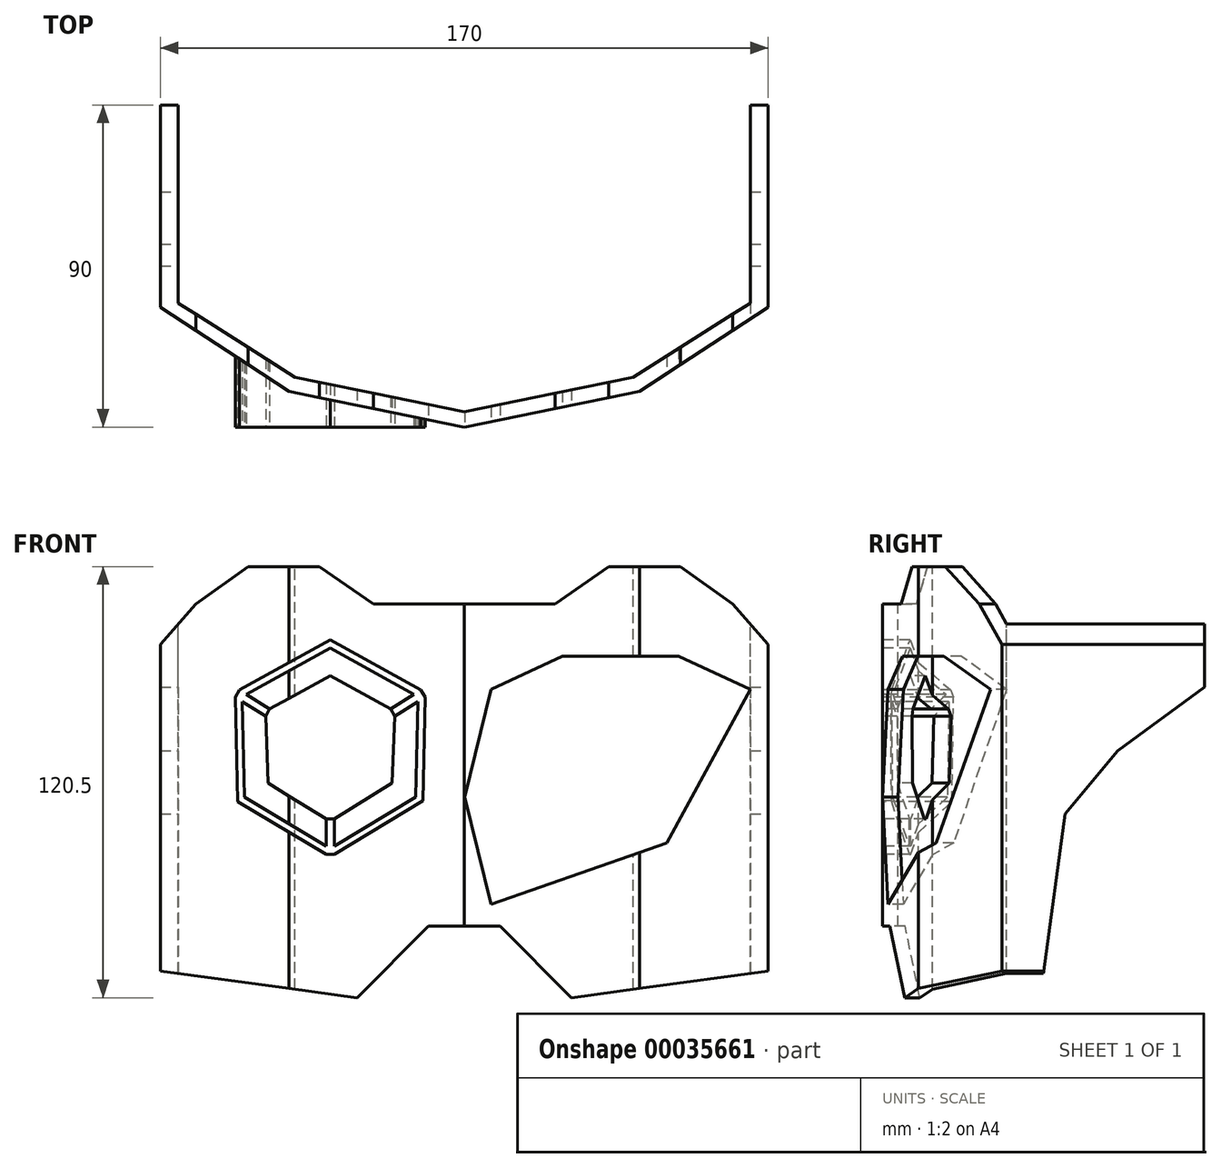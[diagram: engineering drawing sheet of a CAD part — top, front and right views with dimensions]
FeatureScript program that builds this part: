
annotation { "Feature Type Name" : "Feature", "Feature Type Description" : "" }
export const myFeature = defineFeature(function(context is Context, id is Id, definition is map)
    precondition{}
    {
        {
            var Q0;
            Q0=qCreatedBy(makeId("Front.planeOp"),FACE);
            var sketch = newSketch(context, id + "F0", { "sketchPlane" : qUnion([Q0])});
            skLineSegment(sketch, "E0.bottom", {"start": v(-25.45, 110) * mm, "end": v(25.45, 110) * mm});
            skLineSegment(sketch, "E0.top", {"start": v(-85, 0) * mm, "end": v(85, 0) * mm});
            skLineSegment(sketch, "E0.left", {"start": v(-85, 98.76) * mm, "end": v(-85, 0) * mm});
            skLineSegment(sketch, "E0.right", {"start": v(85, 98.76) * mm, "end": v(85, 0) * mm});
            skLineSegment(sketch, "E1", {"start": v(-85, 98.76) * mm, "end": v(-75.07, 110) * mm});
            skLineSegment(sketch, "E2", {"start": v(75.07, 110) * mm, "end": v(85, 98.76) * mm});
            skLineSegment(sketch, "E3", {"start": v(-85, 7.5) * mm, "end": v(-30, 0) * mm});
            skLineSegment(sketch, "E4", {"start": v(-30, 0) * mm, "end": v(-10, 20) * mm});
            skLineSegment(sketch, "E5", {"start": v(-10, 20) * mm, "end": v(10, 20) * mm});
            skLineSegment(sketch, "E6", {"start": v(10, 20) * mm, "end": v(30, 0) * mm});
            skLineSegment(sketch, "E7", {"start": v(30, 0) * mm, "end": v(85, 7.5) * mm});
            skLineSegment(sketch, "E8", {"start": v(-75.07, 110) * mm, "end": v(-60.45, 120.5) * mm});
            skLineSegment(sketch, "E9", {"start": v(-60.45, 120.5) * mm, "end": v(-40.45, 120.5) * mm});
            skLineSegment(sketch, "E10", {"start": v(-40.45, 120.5) * mm, "end": v(-25.45, 110) * mm});
            skLineSegment(sketch, "E11", {"start": v(25.45, 110) * mm, "end": v(40.45, 120.5) * mm});
            skLineSegment(sketch, "E12", {"start": v(40.45, 120.5) * mm, "end": v(60.45, 120.5) * mm});
            skLineSegment(sketch, "E13", {"start": v(60.45, 120.5) * mm, "end": v(75.07, 110) * mm});
            skSolve(sketch);
        }
        {
            var Q0;
            Q0=makeQuery(id+"F0.imprint","IMPRINT",FACE,{"disambiguationData":[TD([[makeQuery(id+"F0.imprint","IMPRINT",EDGE,{"derivedFrom":sQuery(id+"F0.wireOp",EDGE,"E0.bottom")}),-1.0]])]});
            extrude(context, id + "F1", {"entities" : qUnion([Q0]), "oppositeDirection" : true, "depth" : 90 * mm});
        }
        {
            var Q0;
            Q0=makeQuery(id+"F1.opExtrude","CAP_FACE",FACE,{"disambiguationData":[OSD([sQuery(id+"F0.wireOp",EDGE,"E0.bottom"),sQuery(id+"F0.wireOp",EDGE,"E0.left"),sQuery(id+"F0.wireOp",EDGE,"E0.right"),sQuery(id+"F0.wireOp",EDGE,"E1"),sQuery(id+"F0.wireOp",EDGE,"E2"),sQuery(id+"F0.wireOp",EDGE,"E3"),sQuery(id+"F0.wireOp",EDGE,"E4"),sQuery(id+"F0.wireOp",EDGE,"E5"),sQuery(id+"F0.wireOp",EDGE,"E6"),sQuery(id+"F0.wireOp",EDGE,"E7"),sQuery(id+"F0.wireOp",EDGE,"E8"),sQuery(id+"F0.wireOp",EDGE,"E9"),sQuery(id+"F0.wireOp",EDGE,"E10"),sQuery(id+"F0.wireOp",EDGE,"E11"),sQuery(id+"F0.wireOp",EDGE,"E12"),sQuery(id+"F0.wireOp",EDGE,"E13")])],"isStart":true});
            var sketch = newSketch(context, id + "F2", { "sketchPlane" : qUnion([Q0])});
            skCircle(sketch, "E14", {"center": v(-37.5, 70) * mm, "radius": 30 * mm, "construction": true});
            skCircle(sketch, "E15", {"center": v(-37.5, 70) * mm, "radius": 20 * mm, "construction": true});
            skLineSegment(sketch, "E16", {"start": v(-20.58, 80.67) * mm, "end": v(-14.08, 84.77) * mm});
            skPoint(sketch, "E17", {"position": v(-7.5, 70) * mm});
            skPoint(sketch, "E18", {"position": v(-67.5, 70) * mm});
            skLineSegment(sketch, "E19", {"start": v(7.5, 86.14) * mm, "end": v(27.5, 95.5) * mm});
            skLineSegment(sketch, "E20", {"start": v(27.5, 95.5) * mm, "end": v(60, 95.5) * mm});
            skLineSegment(sketch, "E21", {"start": v(60, 95.5) * mm, "end": v(80, 86.14) * mm});
            skLineSegment(sketch, "E22", {"start": v(-19.46, 78.64) * mm, "end": v(-12.93, 82.76) * mm});
            skLineSegment(sketch, "E23", {"start": v(-54.42, 80.67) * mm, "end": v(-60.92, 84.77) * mm});
            skLineSegment(sketch, "E24", {"start": v(-55.53, 78.65) * mm, "end": v(-62.07, 82.77) * mm});
            skLineSegment(sketch, "E25", {"start": v(-36.34, 50.03) * mm, "end": v(-36.34, 42.33) * mm});
            skLineSegment(sketch, "E26", {"start": v(-38.65, 50.03) * mm, "end": v(-38.65, 42.33) * mm});
            skArc(sketch, "E27.0", {"start": v(-62.07, 82.77) * mm, "mid": v(-61.46, 56.12) * mm, "end": v(-38.66, 42.33) * mm, "construction": true});
            skPoint(sketch, "E28.orphan", {"position": v(-64.03, 84) * mm});
            skPoint(sketch, "E29.orphan", {"position": v(-62.87, 86) * mm});
            skArc(sketch, "E30.trimOffspring", {"start": v(-14.08, 84.77) * mm, "mid": v(-37.5, 97.69) * mm, "end": v(-60.92, 84.77) * mm, "construction": true});
            skPoint(sketch, "E31.orphan", {"position": v(-12.12, 86) * mm});
            skPoint(sketch, "E32.orphan", {"position": v(-10.97, 84) * mm});
            skPoint(sketch, "E33.orphan", {"position": v(-36.35, 40.02) * mm});
            skPoint(sketch, "E34.orphan", {"position": v(-38.66, 40.02) * mm});
            skArc(sketch, "E35.trimOffspring", {"start": v(-36.35, 42.33) * mm, "mid": v(-13.54, 56.12) * mm, "end": v(-12.93, 82.76) * mm, "construction": true});
            skLineSegment(sketch, "E36", {"start": v(-37.5, 70) * mm, "end": v(-37.5, 97.7) * mm, "construction": true});
            skLineSegment(sketch, "E37", {"start": v(-37.5, 70) * mm, "end": v(-13.54, 56.12) * mm, "construction": true});
            skLineSegment(sketch, "E38", {"start": v(-37.5, 70) * mm, "end": v(-61.46, 56.12) * mm, "construction": true});
            skLineSegment(sketch, "E39", {"start": v(7.5, 26.14) * mm, "end": v(56.63, 43.24) * mm});
            skLineSegment(sketch, "E40", {"start": v(56.63, 43.24) * mm, "end": v(80, 86.14) * mm});
            skLineSegment(sketch, "E41", {"start": v(7.5, 26.14) * mm, "end": v(0.16, 56.14) * mm});
            skLineSegment(sketch, "E42", {"start": v(0.16, 56.14) * mm, "end": v(7.5, 86.14) * mm});
            skLineSegment(sketch, "E43", {"start": v(-36.35, 42.33) * mm, "end": v(-13.54, 56.12) * mm});
            skLineSegment(sketch, "E44", {"start": v(-12.93, 82.76) * mm, "end": v(-13.54, 56.12) * mm});
            skLineSegment(sketch, "E45", {"start": v(-14.08, 84.77) * mm, "end": v(-37.5, 97.7) * mm});
            skLineSegment(sketch, "E46", {"start": v(-60.92, 84.77) * mm, "end": v(-37.5, 97.7) * mm});
            skLineSegment(sketch, "E47", {"start": v(-38.66, 42.33) * mm, "end": v(-61.46, 56.12) * mm});
            skLineSegment(sketch, "E48", {"start": v(-61.46, 56.12) * mm, "end": v(-62.07, 82.77) * mm});
            skLineSegment(sketch, "E49", {"start": v(-64.03, 84) * mm, "end": v(-63.36, 54.8) * mm});
            skLineSegment(sketch, "E50", {"start": v(-63.36, 54.8) * mm, "end": v(-38.66, 40.02) * mm});
            skLineSegment(sketch, "E51", {"start": v(-36.35, 40.02) * mm, "end": v(-11.5, 55.05) * mm});
            skLineSegment(sketch, "E52", {"start": v(-11.5, 55.05) * mm, "end": v(-10.97, 84) * mm});
            skLineSegment(sketch, "E53", {"start": v(-62.87, 86) * mm, "end": v(-37.5, 100) * mm});
            skLineSegment(sketch, "E54", {"start": v(-37.5, 100) * mm, "end": v(-12.12, 86) * mm});
            skLineSegment(sketch, "E55", {"start": v(-36.35, 50.03) * mm, "end": v(-20.2, 59.98) * mm});
            skLineSegment(sketch, "E56", {"start": v(-20.2, 59.98) * mm, "end": v(-19.46, 78.64) * mm});
            skLineSegment(sketch, "E57", {"start": v(-38.66, 50.03) * mm, "end": v(-54.8, 59.98) * mm});
            skLineSegment(sketch, "E58", {"start": v(-54.8, 59.98) * mm, "end": v(-55.53, 78.65) * mm});
            skLineSegment(sketch, "E59", {"start": v(-54.42, 80.67) * mm, "end": v(-37.5, 90) * mm});
            skLineSegment(sketch, "E60", {"start": v(-37.5, 90) * mm, "end": v(-20.58, 80.67) * mm});
            skLineSegment(sketch, "E61", {"start": v(-55.53, 78.65) * mm, "end": v(-54.42, 80.67) * mm, "construction": true});
            skLineSegment(sketch, "E62", {"start": v(-20.58, 80.67) * mm, "end": v(-19.46, 78.64) * mm, "construction": true});
            skLineSegment(sketch, "E63", {"start": v(-38.66, 50.03) * mm, "end": v(-36.35, 50.03) * mm});
            skLineSegment(sketch, "E64", {"start": v(-55.53, 78.65) * mm, "end": v(-54.42, 80.67) * mm});
            skLineSegment(sketch, "E65", {"start": v(-20.58, 80.67) * mm, "end": v(-19.46, 78.64) * mm});
            skLineSegment(sketch, "E66", {"start": v(-38.66, 40.02) * mm, "end": v(-36.35, 40.02) * mm});
            skLineSegment(sketch, "E67", {"start": v(-10.97, 84) * mm, "end": v(-12.12, 86) * mm});
            skLineSegment(sketch, "E68", {"start": v(-64.03, 84) * mm, "end": v(-62.87, 86) * mm});
            skSolve(sketch);
        }
        {
            var Q0;
            Q0=makeQuery(id+"F2.imprint","IMPRINT",FACE,{"disambiguationData":[TD([[makeQuery(id+"F2.imprint","IMPRINT",EDGE,{"derivedFrom":sQuery(id+"F2.wireOp",EDGE,"E19")}),-1.0]])]});
            var Q1;
            Q1=makeQuery(id+"F1.opExtrude","CAP_FACE",FACE,{"disambiguationData":[OSD([sQuery(id+"F0.wireOp",EDGE,"E0.bottom"),sQuery(id+"F0.wireOp",EDGE,"E0.left"),sQuery(id+"F0.wireOp",EDGE,"E0.right"),sQuery(id+"F0.wireOp",EDGE,"E1"),sQuery(id+"F0.wireOp",EDGE,"E2"),sQuery(id+"F0.wireOp",EDGE,"E3"),sQuery(id+"F0.wireOp",EDGE,"E4"),sQuery(id+"F0.wireOp",EDGE,"E5"),sQuery(id+"F0.wireOp",EDGE,"E6"),sQuery(id+"F0.wireOp",EDGE,"E7"),sQuery(id+"F0.wireOp",EDGE,"E8"),sQuery(id+"F0.wireOp",EDGE,"E9"),sQuery(id+"F0.wireOp",EDGE,"E10"),sQuery(id+"F0.wireOp",EDGE,"E11"),sQuery(id+"F0.wireOp",EDGE,"E12"),sQuery(id+"F0.wireOp",EDGE,"E13")])],"isStart":false});
            extrude(context, id + "F3", {"entities" : qUnion([Q0]), "operationType" : NewBodyOperationType.REMOVE, "endBound" : BoundingType.UP_TO_SURFACE, "oppositeDirection" : true, "endBoundEntityFace" : qUnion([Q1]), "depth" : 25 * mm});
        }
        {
            var Q0;
            Q0=makeQuery(id+"F2.imprint","IMPRINT",FACE,{"disambiguationData":[TD([[makeQuery(id+"F2.imprint","IMPRINT",EDGE,{"derivedFrom":sQuery(id+"F2.wireOp",EDGE,"E55")}),1.0]])]});
            var Q1;
            Q1=makeQuery(id+"F1.opExtrude","CAP_FACE",FACE,{"disambiguationData":[OSD([sQuery(id+"F0.wireOp",EDGE,"E0.bottom"),sQuery(id+"F0.wireOp",EDGE,"E0.left"),sQuery(id+"F0.wireOp",EDGE,"E0.right"),sQuery(id+"F0.wireOp",EDGE,"E1"),sQuery(id+"F0.wireOp",EDGE,"E2"),sQuery(id+"F0.wireOp",EDGE,"E3"),sQuery(id+"F0.wireOp",EDGE,"E4"),sQuery(id+"F0.wireOp",EDGE,"E5"),sQuery(id+"F0.wireOp",EDGE,"E6"),sQuery(id+"F0.wireOp",EDGE,"E7"),sQuery(id+"F0.wireOp",EDGE,"E8"),sQuery(id+"F0.wireOp",EDGE,"E9"),sQuery(id+"F0.wireOp",EDGE,"E10"),sQuery(id+"F0.wireOp",EDGE,"E11"),sQuery(id+"F0.wireOp",EDGE,"E12"),sQuery(id+"F0.wireOp",EDGE,"E13")])],"isStart":false});
            extrude(context, id + "F4", {"entities" : qUnion([Q0]), "operationType" : NewBodyOperationType.REMOVE, "endBound" : BoundingType.UP_TO_SURFACE, "oppositeDirection" : true, "endBoundEntityFace" : qUnion([Q1]), "depth" : 25 * mm});
        }
        {
            var Q0;
            Q0=makeQuery(id+"F1.opExtrude","SWEPT_FACE",FACE,{"disambiguationData":[OSD([sQuery(id+"F0.wireOp",EDGE,"E9")])]});
            var sketch = newSketch(context, id + "F5", { "sketchPlane" : qUnion([Q0])});
            skLineSegment(sketch, "E69", {"start": v(85, 33.43) * mm, "end": v(85, 90) * mm});
            skLineSegment(sketch, "E70", {"start": v(85, 90) * mm, "end": v(80, 90) * mm});
            skLineSegment(sketch, "E71", {"start": v(80, 90) * mm, "end": v(80, 34.67) * mm});
            skLineSegment(sketch, "E72", {"start": v(-85, 90) * mm, "end": v(-80, 90) * mm});
            skLineSegment(sketch, "E73", {"start": v(-80, 90) * mm, "end": v(-80, 34.67) * mm});
            skLineSegment(sketch, "E74", {"start": v(-85, 90) * mm, "end": v(-85, 33.43) * mm});
            skLineSegment(sketch, "E75", {"start": v(-85, 33.43) * mm, "end": v(-48.99, 10.02) * mm});
            skLineSegment(sketch, "E76", {"start": v(-48.99, 10.02) * mm, "end": v(0, 0) * mm});
            skLineSegment(sketch, "E77", {"start": v(0, 0) * mm, "end": v(48.99, 10.02) * mm});
            skLineSegment(sketch, "E78", {"start": v(48.99, 10.02) * mm, "end": v(85, 33.43) * mm});
            skLineSegment(sketch, "E79", {"start": v(-80, 34.67) * mm, "end": v(-47.3, 13.95) * mm});
            skLineSegment(sketch, "E80", {"start": v(-47.3, 13.95) * mm, "end": v(0, 4.28) * mm});
            skLineSegment(sketch, "E81", {"start": v(0, 4.28) * mm, "end": v(47.3, 13.95) * mm});
            skLineSegment(sketch, "E82", {"start": v(47.3, 13.95) * mm, "end": v(80, 34.67) * mm});
            skSolve(sketch);
        }
        {
            var Q0;
            Q0=qSketchRegion(id+"F5",true);
            var Q1;
            Q1=qCreatedBy(makeId("Top.planeOp"),FACE);
            extrude(context, id + "F6", {"entities" : qUnion([Q0]), "operationType" : NewBodyOperationType.INTERSECT, "endBound" : BoundingType.UP_TO_SURFACE, "oppositeDirection" : true, "endBoundEntityFace" : qUnion([Q1]), "depth" : 25 * mm});
        }
        {
            var Q0;
            Q0=makeQuery(id+"F2.imprint","IMPRINT",FACE,{"disambiguationData":[TD([[makeQuery(id+"F2.imprint","IMPRINT",EDGE,{"derivedFrom":sQuery(id+"F2.wireOp",EDGE,"E16")}),-1.0]])]});
            var Q1;
            Q1=makeQuery(id+"F1.opExtrude","SWEPT_BODY",BODY,{"disambiguationData":[OSD([sQuery(id+"F0.wireOp",EDGE,"E0.bottom"),sQuery(id+"F0.wireOp",EDGE,"E0.left"),sQuery(id+"F0.wireOp",EDGE,"E0.right"),sQuery(id+"F0.wireOp",EDGE,"E1"),sQuery(id+"F0.wireOp",EDGE,"E2"),sQuery(id+"F0.wireOp",EDGE,"E3"),sQuery(id+"F0.wireOp",EDGE,"E4"),sQuery(id+"F0.wireOp",EDGE,"E5"),sQuery(id+"F0.wireOp",EDGE,"E6"),sQuery(id+"F0.wireOp",EDGE,"E7"),sQuery(id+"F0.wireOp",EDGE,"E8"),sQuery(id+"F0.wireOp",EDGE,"E9"),sQuery(id+"F0.wireOp",EDGE,"E10"),sQuery(id+"F0.wireOp",EDGE,"E11"),sQuery(id+"F0.wireOp",EDGE,"E12"),sQuery(id+"F0.wireOp",EDGE,"E13")])]});
            extrude(context, id + "F7", {"entities" : qUnion([Q0]), "operationType" : NewBodyOperationType.ADD, "endBound" : BoundingType.UP_TO_NEXT, "oppositeDirection" : true, "endBoundEntityBody" : qUnion([Q1]), "depth" : 2.31 * mm});
        }
        {
            var Q0;
            Q0=makeQuery(id+"F1.opExtrude","SWEPT_FACE",FACE,{"disambiguationData":[OSD([sQuery(id+"F0.wireOp",EDGE,"E0.right")])]});
            var sketch = newSketch(context, id + "F8", { "sketchPlane" : qUnion([Q0])});
            skLineSegment(sketch, "E83", {"start": v(90, 6.82) * mm, "end": v(45, 6.82) * mm});
            skLineSegment(sketch, "E84", {"start": v(90, 6.82) * mm, "end": v(90, 86.82) * mm});
            skLineSegment(sketch, "E85", {"start": v(45, 6.82) * mm, "end": v(51.09, 51.4) * mm});
            skLineSegment(sketch, "E86", {"start": v(51.09, 51.4) * mm, "end": v(65.8, 69.08) * mm});
            skLineSegment(sketch, "E87", {"start": v(65.8, 69.08) * mm, "end": v(90, 86.82) * mm});
            skSolve(sketch);
        }
        {
            var Q0;
            Q0=qSketchRegion(id+"F8",true);
            var Q1;
            Q1=makeQuery(id+"F1.opExtrude","SWEPT_FACE",FACE,{"disambiguationData":[OSD([sQuery(id+"F0.wireOp",EDGE,"E0.left")])]});
            extrude(context, id + "F9", {"entities" : qUnion([Q0]), "operationType" : NewBodyOperationType.REMOVE, "endBound" : BoundingType.UP_TO_SURFACE, "oppositeDirection" : true, "endBoundEntityFace" : qUnion([Q1]), "depth" : 25 * mm});
        }
    });
